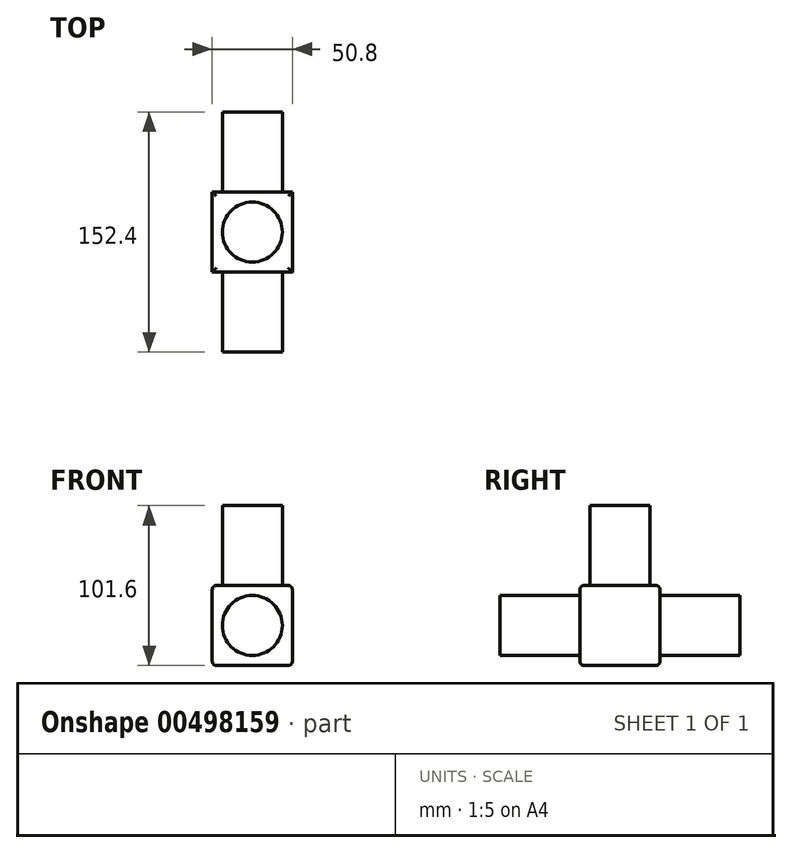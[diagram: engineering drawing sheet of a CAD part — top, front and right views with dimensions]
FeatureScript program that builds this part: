
annotation { "Feature Type Name" : "Feature", "Feature Type Description" : "" }
export const myFeature = defineFeature(function(context is Context, id is Id, definition is map)
    precondition{}
    {
        {
            var Q0;
            Q0=qCreatedBy(makeId("Front.planeOp"),FACE);
            var sketch = newSketch(context, id + "F0", { "sketchPlane" : qUnion([Q0])});
            skLineSegment(sketch, "E0.bottom", {"start": v(0, 0) * mm, "end": v(50.8, 0) * mm});
            skLineSegment(sketch, "E0.top", {"start": v(0, 50.8) * mm, "end": v(50.8, 50.8) * mm});
            skLineSegment(sketch, "E0.left", {"start": v(0, 0) * mm, "end": v(0, 50.8) * mm});
            skLineSegment(sketch, "E0.right", {"start": v(50.8, 0) * mm, "end": v(50.8, 50.8) * mm});
            skCircle(sketch, "E1", {"center": v(25.4, 25.4) * mm, "radius": 19.05 * mm});
            skPoint(sketch, "E2.orphan", {"position": v(0, 25.4) * mm});
            skPoint(sketch, "E3.start.orphan", {"position": v(25.4, 50.8) * mm});
            skPoint(sketch, "E4.trimOffspring.end.orphan", {"position": v(25.4, 0) * mm});
            skPoint(sketch, "E5.end.orphan", {"position": v(50.8, 25.4) * mm});
            skSolve(sketch);
        }
        {
            var Q0;
            Q0=makeQuery(id+"F0.imprint","IMPRINT",FACE,{"disambiguationData":[TD([[makeQuery(id+"F0.imprint","IMPRINT",EDGE,{"derivedFrom":sQuery(id+"F0.wireOp",EDGE,"E1")}),1.0]])]});
            extrude(context, id + "F1", {"entities" : qUnion([Q0]), "depth" : 101.6 * mm});
        }
        {
            var Q0;
            Q0 = qSketchRegion(id + "F0", true);
            extrude(context, id + "F2", {"entities" : qUnion([Q0]), "operationType" : NewBodyOperationType.ADD, "depth" : 50.8 * mm});
        }
        {
            var Q0;
            Q0=makeQuery(id+"F2.opExtrude","SWEPT_FACE",FACE,{"disambiguationData":[OSD([sQuery(id+"F0.wireOp",EDGE,"E0.top")])]});
            var sketch = newSketch(context, id + "F3", { "sketchPlane" : qUnion([Q0])});
            skCircle(sketch, "E6", {"center": v(25.4, -25.4) * mm, "radius": 19.05 * mm});
            skPoint(sketch, "E7.start.orphan", {"position": v(25.4, 0) * mm});
            skPoint(sketch, "E8.trimOffspring.end.orphan", {"position": v(50.8, -25.4) * mm});
            skPoint(sketch, "E9.trimOffspring.end.orphan", {"position": v(25.4, -50.8) * mm});
            skPoint(sketch, "E10.start.orphan", {"position": v(0, -25.4) * mm});
            skSolve(sketch);
        }
        {
            var Q0;
            Q0=makeQuery(id+"F3.imprint","IMPRINT",FACE,{"disambiguationData":[TD([[makeQuery(id+"F3.imprint","IMPRINT",EDGE,{"derivedFrom":sQuery(id+"F3.wireOp",EDGE,"E6")}),1.0]])]});
            extrude(context, id + "F4", {"entities" : qUnion([Q0]), "operationType" : NewBodyOperationType.ADD, "depth" : 50.8 * mm});
        }
        {
            var Q0;
            {var subQ0=sQuery(id+"F0.wireOp",EDGE,"E1");Q0=makeQuery(id+"F2.boolean.opBoolean","MERGE",FACE,{"derivedFrom":[makeQuery(id+"F1.opExtrude","CAP_FACE",FACE,{"disambiguationData":[OSD([subQ0])],"isStart":true}),makeQuery(id+"F2.opExtrude","CAP_FACE",FACE,{"disambiguationData":[OSD([sQuery(id+"F0.wireOp",EDGE,"E0.bottom"),sQuery(id+"F0.wireOp",EDGE,"E0.top"),sQuery(id+"F0.wireOp",EDGE,"E0.left"),sQuery(id+"F0.wireOp",EDGE,"E0.right"),subQ0])],"isStart":true})]});}
            var sketch = newSketch(context, id + "F5", { "sketchPlane" : qUnion([Q0])});
            skCircle(sketch, "E11", {"center": v(-25.4, 25.4) * mm, "radius": 19.05 * mm});
            skPoint(sketch, "E12.trimOffspring.end.orphan", {"position": v(-50.8, 25.4) * mm});
            skPoint(sketch, "E13.start.orphan", {"position": v(-25.4, 0) * mm});
            skPoint(sketch, "E14.trimOffspring.end.orphan", {"position": v(-25.4, 50.8) * mm});
            skPoint(sketch, "E15.start.orphan", {"position": v(0, 25.4) * mm});
            skSolve(sketch);
        }
        {
            var Q0;
            Q0=makeQuery(id+"F5.imprint","IMPRINT",FACE,{"disambiguationData":[TD([[makeQuery(id+"F5.imprint","IMPRINT",EDGE,{"derivedFrom":sQuery(id+"F5.wireOp",EDGE,"E11")}),1.0]])]});
            extrude(context, id + "F6", {"entities" : qUnion([Q0]), "operationType" : NewBodyOperationType.ADD, "depth" : 50.8 * mm});
        }
        {
            var Q0;
            Q0=makeQuery(id+"F2.opExtrude","CAP_EDGE",EDGE,{"disambiguationData":[OSD([sQuery(id+"F0.wireOp",EDGE,"E0.top")])],"isStart":false});
            var Q1;
            Q1=makeQuery(id+"F2.opExtrude","SWEPT_EDGE",EDGE,{"disambiguationData":[OSD([sQuery(id+"F0.wireOp",EDGE,"E0.top"),sQuery(id+"F0.wireOp",EDGE,"E0.right")])]});
            var Q2;
            Q2=makeQuery(id+"F2.opExtrude","CAP_EDGE",EDGE,{"disambiguationData":[OSD([sQuery(id+"F0.wireOp",EDGE,"E0.top")])],"isStart":true});
            var Q3;
            Q3=makeQuery(id+"F2.opExtrude","SWEPT_EDGE",EDGE,{"disambiguationData":[OSD([sQuery(id+"F0.wireOp",EDGE,"E0.top"),sQuery(id+"F0.wireOp",EDGE,"E0.left")])]});
            fillet(context, id + "F7", {"entities" : qUnion([Q0, Q1, Q2, Q3]), "radius" : 2.54 * mm, "tangentPropagation" : true, "allowEdgeOverflow" : false});
        }
        {
            var Q0;
            Q0=makeQuery(id+"F2.opExtrude","SWEPT_EDGE",EDGE,{"disambiguationData":[OSD([sQuery(id+"F0.wireOp",EDGE,"E0.bottom"),sQuery(id+"F0.wireOp",EDGE,"E0.right")])]});
            var Q1;
            Q1=makeQuery(id+"F2.opExtrude","CAP_EDGE",EDGE,{"disambiguationData":[OSD([sQuery(id+"F0.wireOp",EDGE,"E0.bottom")])],"isStart":false});
            var Q2;
            Q2=makeQuery(id+"F2.opExtrude","CAP_EDGE",EDGE,{"disambiguationData":[OSD([sQuery(id+"F0.wireOp",EDGE,"E0.bottom")])],"isStart":true});
            var Q3;
            Q3=makeQuery(id+"F2.opExtrude","SWEPT_EDGE",EDGE,{"disambiguationData":[OSD([sQuery(id+"F0.wireOp",EDGE,"E0.bottom"),sQuery(id+"F0.wireOp",EDGE,"E0.left")])]});
            fillet(context, id + "F8", {"entities" : qUnion([Q0, Q1, Q2, Q3]), "radius" : 2.54 * mm, "tangentPropagation" : true, "allowEdgeOverflow" : false});
        }
    });
